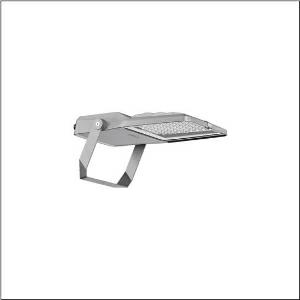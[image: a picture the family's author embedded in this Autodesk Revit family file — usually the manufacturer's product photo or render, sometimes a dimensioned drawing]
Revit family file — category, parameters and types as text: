
# Revit family: floodlight_fl_21_iq_mini___rs12_5xa7772b4b1a_ec65
name_source: partatom
category: Lighting Fixtures
units: mm (PartAtom-declared; Revit-internal decimal feet)

## family parameters
Cut with Voids When Loaded = No
Host = Face
Light Source = No
Part Type = Normal
Room Calculation Point = No
Round Connector Dimension = Use Diameter
Shared = No

## types (1)
- --- (1 x LED, 6560 lm, 45.5 W, 4000K)
    Apparent Load = 46 VA
    CIE Flux Codes = 79 92 99 100 100
    Color Rendering = 70
    Color Temperature = 4000K
    Default Elevation = 1800 mm
    Description = Floodlight FL 21 iQ mini, floodlight, primary light control with lens, of PMMA, primary optical cover: protective disc, of toughened safety glass, transparent, light distribution: RS12, light emission: direct distribution, installation type: surface-mounted, lamps: LED, High Power LED, rated values: 6.560lm | 45,5W | 144,2lm/W (begin service life); end service life: 6.560lm | 48W; at 50% lumin. flux: 3.280lm | 21,5W | 152,6lm/W, colour temperature: 4000K, colour rendering: CRI > 70, light colour: 740, light setting 1 begin service life: 100% | 6.560lm | 45,5W | 144,2lm/W | 4.000K, light setting 1 end service life: 48W, further light settings possible, control: Street-Remote, Auto-Match, Temp-Guard, Night-Set, Smart-Wire, Desk-Remote (wireless, voltage-free reading and setting of iQ features in the workshop via application-optimized NFC function/RFID function), optimised constant luminous flux control (CLO 2.0), pre-setting: linear dimming characteristic, with terminal, 6-pole, mains connection: 220..240V, AC, 50/60Hz, luminaire housing, of diecast aluminium, powder-coated, SITECO metallic grey (DB 702S), corrosivity category C5 mid according to DIN EN ISO 12944suitable for swimming poolschlorine-resistant, sealing non-destructively replaceable, mounting bracket, of steel, galvanised, powder-coated, SITECO metallic grey (DB 702S), protection rating (complete): IP66, insulation class (complete): insulation class II (safety insulation), certification: CE, ENEC, VDE, protection symbol: D, impact resistance: IK08, permissible operating ambient temperature: -40..+40°C, permissible operating ambient temperature for outdoor applications: -40..+50°C, standard: DIN EN 12944, LABS conformity tested according to VDMA 24364:2018-05, packaging unit: 1 piece

Light Distribution: RS12
    Height = 70 mm
    Lamp = 1 x LED
    Lamp Light Flux = 6560 lm
    Lamp Power = 45.5 W
    Lamp count = 1
    Length = 485 mm
    Luminous efficacy = 144 lm/W
    Manufacturer = Siteco
    ModVariant = No
    Model = 5XA7772B4B1A
    Number of Poles = 1
    OnlyDefault = Yes
    Power Factor = 1
    Product Name = Floodlight FL 21 iQ mini | RS12
    Product group = floodlight | pylon annexe
    ProductGroupID = 6201
    Protection Class = Protection class II
    Protection Degree = IP 66
    RLX_Detail_Level = 1
    RLX_Emergency_Light_Flux = 0 lm
    RLX_Emergency_Type = 0
    RLX_Emergency_Type_DB = No
    RlxData = <blob elided: 91141 chars, md5=36b1fdc6>
    Socket = socket
    Standby Power = 0 W
    System Light Flux = 6560 lm
    System Power = 46 W
    Type Comments = factory setting: luminous flux: 100 % | dim-lin: 254 | 463 mA
    Type Image = l_1006845.jpg
    URL = http://relux.com
    VarID = @adj_167293
    Voltage = 0 V
    Weight = 0.00 kg
    Width = 337 mm

## geometry (parser evidence)
native form markers: Blend x4, Sweep x14
no freeform markers — native parametric forms only
